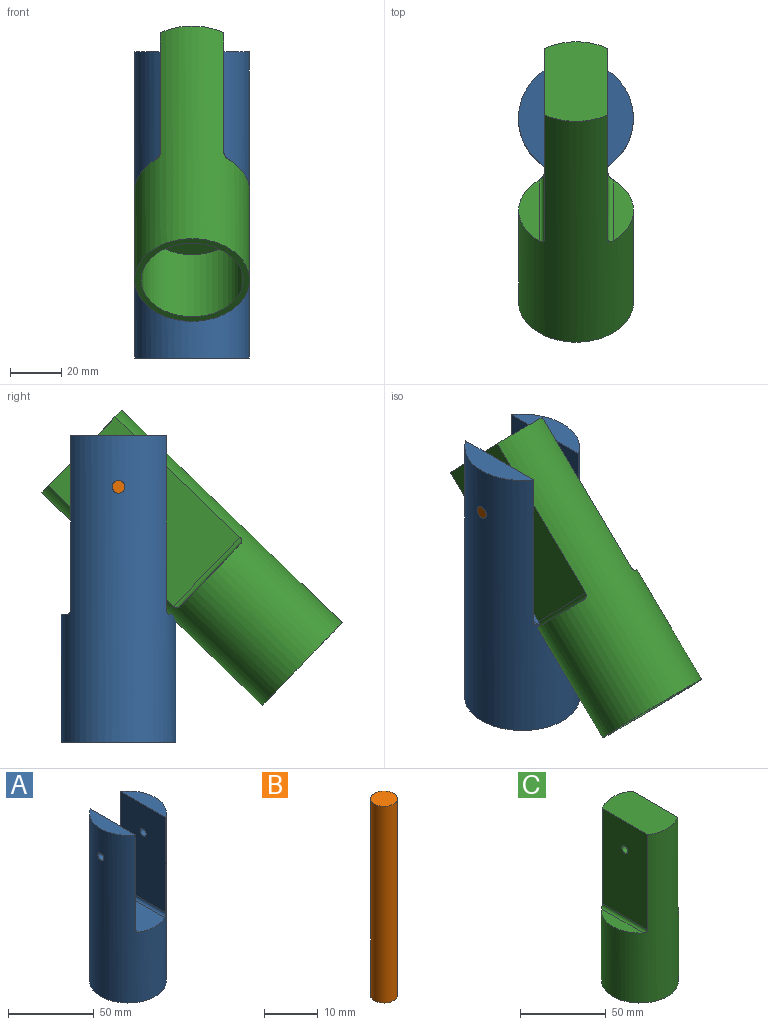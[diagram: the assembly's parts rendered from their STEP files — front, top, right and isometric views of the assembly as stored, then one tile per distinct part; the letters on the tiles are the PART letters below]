
ASSEMBLY  parts=3 mates=2
PART A: 13 faces, bbox 45x45x120 mm
  f0: cylinder r=22.5mm len=120mm, axis (0,0,-1), area 13218.5mm2, adj f1,f2,f3,f4,f5,f6,f9,f10
  f1: plane 37.42x10mm, normal (0,0,1), area 263.2mm2, adj f0,f5
  f2: plane 37.42x10mm, normal (0,0,1), area 263.2mm2, adj f0,f4
  f3: plane 45x45mm, normal (0,0,-1), area 333.8mm2, adj f0,f7
  f4: plane 68x37.42mm, normal (1,0,0), area 2524.7mm2, adj f0,f2,f10,f11
  f5: plane 68x37.42mm, normal (-1,0,0), area 2524.7mm2, adj f0,f1,f9,f12
  f6: plane 45x21mm, normal (0,0,1), area 909.5mm2, adj f0,f11,f12
  f7: cylinder r=20mm len=40mm, axis (0,0,-1), area 4398.2mm2, adj f3,f8
  f8: plane 40x40mm, normal (0,0,-1), area 1256.6mm2, adj f7
  f9: cylinder r=2.5mm len=10mm, axis (1,0,0), area 156mm2, adj f0,f5
  f10: cylinder r=2.5mm len=10mm, axis (1,0,0), area 156mm2, adj f0,f4
  f11: cylinder r=2mm len=39.8mm, axis (0,-1,0), area 120.4mm2, adj f0,f4,f6
  f12: cylinder r=2mm len=39.8mm, axis (0,1,0), area 120.4mm2, adj f0,f5,f6
PART B: 3 faces, bbox 5x5x45 mm
  f0: cylinder r=2.5mm len=45mm, axis (0,0,-1), area 706.9mm2, adj f1,f2
  f1: plane 5x5mm, normal (0,0,1), area 19.6mm2, adj f0
  f2: plane 5x5mm, normal (0,0,-1), area 19.6mm2, adj f0
PART C: 12 faces, bbox 45x45x120 mm
  f0: plane 45x25mm, normal (0,0,1), area 1064.1mm2, adj f1,f3,f5
  f1: cylinder r=22.5mm len=120mm, axis (0,0,-1), area 10783.7mm2, adj f0,f2,f3,f4,f5,f6,f10,f11
  f2: plane 45x45mm, normal (0,0,-1), area 333.8mm2, adj f1,f7
  f3: plane 68x37.42mm, normal (-1,0,0), area 2524.7mm2, adj f0,f1,f9,f10
  f4: plane 34.41x8mm, normal (0,0,1), area 191.2mm2, adj f1,f10
  f5: plane 68x37.42mm, normal (1,0,0), area 2524.7mm2, adj f0,f1,f9,f11
  f6: plane 34.41x8mm, normal (0,0,1), area 191.2mm2, adj f1,f11
  f7: cylinder r=20mm len=40mm, axis (0,0,-1), area 4398.2mm2, adj f2,f8
  f8: plane 40x40mm, normal (0,0,-1), area 1256.6mm2, adj f7
  f9: cylinder r=2.5mm len=25mm, axis (1,0,0), area 392.7mm2, adj f3,f5
  f10: cylinder r=2mm len=37.42mm, axis (0,1,0), area 114.3mm2, adj f1,f3,f4
  f11: cylinder r=2mm len=37.42mm, axis (0,-1,0), area 114.3mm2, adj f1,f5,f6
PLACE A t=(-135.08,-41.54,-5.34)mm fixed
PLACE B rot(axis=(0.71,0,0.71),180deg) t=(-157.52,-41.54,94.66)mm
PLACE C rot(axis=(-1,0,0),46deg) t=(-135.02,-113.51,25.23)mm
MATE revolute C.f9 <-> B.f0  axis (1,0,0) through (-135.02,-41.54,94.66)mm
MATE fastened A.f9 <-> B.f0  axis (1,0,0) through (-112.52,-41.54,94.66)mm
